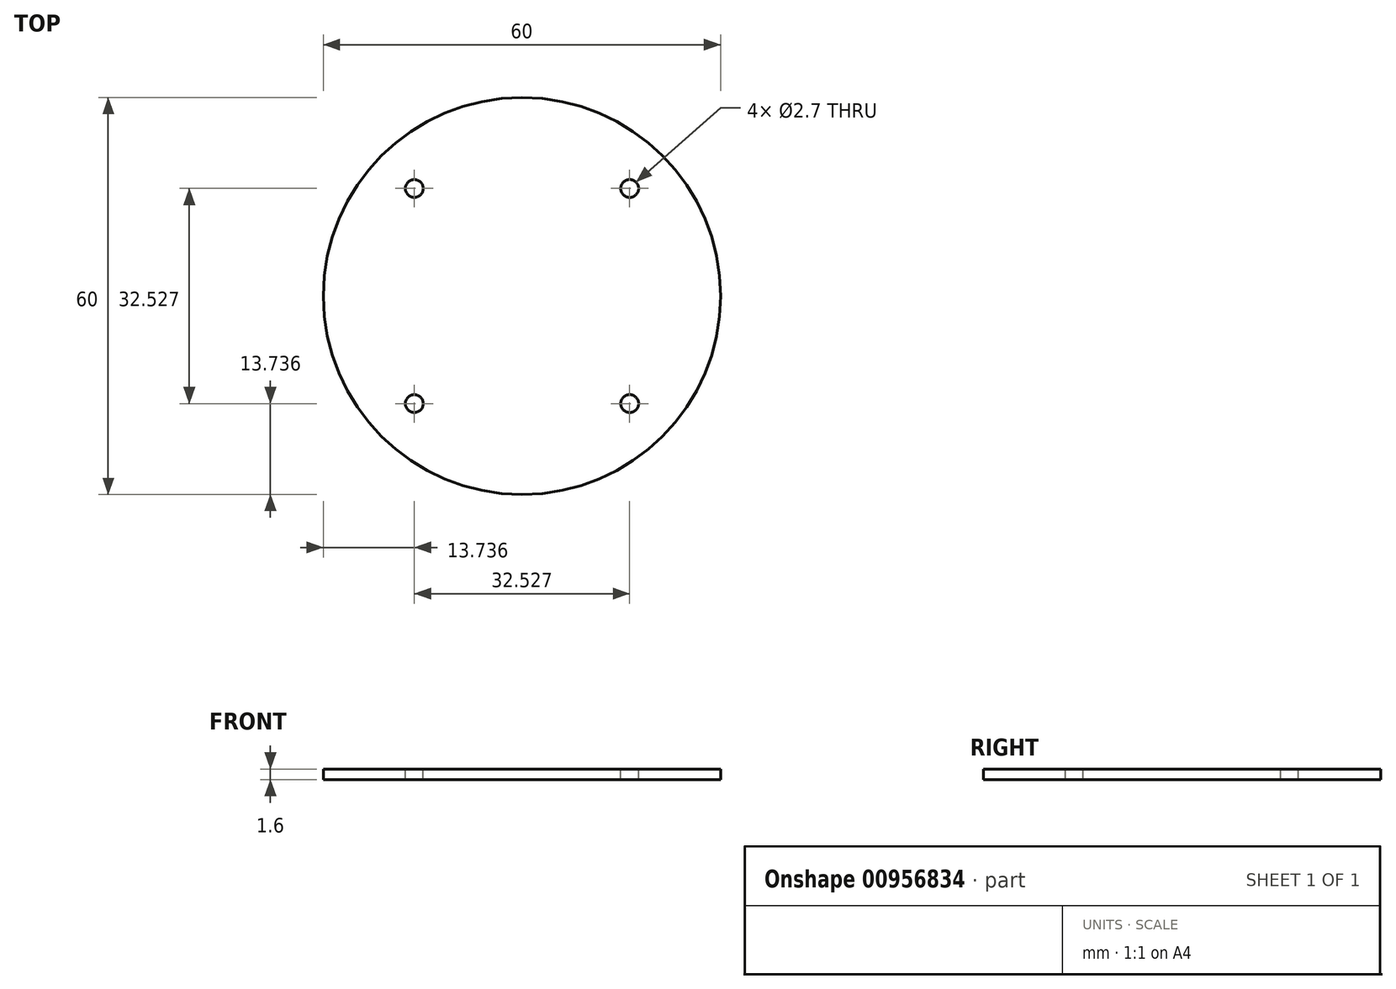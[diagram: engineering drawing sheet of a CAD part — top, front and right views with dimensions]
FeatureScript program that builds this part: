
annotation { "Feature Type Name" : "Feature", "Feature Type Description" : "" }
export const myFeature = defineFeature(function(context is Context, id is Id, definition is map)
    precondition{}
    {
        {
            var Q0;
            Q0=qCreatedBy(makeId("Top.planeOp"),FACE);
            var sketch = newSketch(context, id + "F0", { "sketchPlane" : qUnion([Q0])});
            skCircle(sketch, "E0", {"center": v(0, 0) * mm, "radius": 30 * mm});
            skSolve(sketch);
        }
        {
            var Q0;
            Q0=qSketchRegion(id+"F0",true);
            extrude(context, id + "F1", {"entities" : qUnion([Q0]), "depth" : 1.6 * mm, "offsetDistance" : 25.4 * mm});
        }
        {
            var Q0;
            Q0=makeQuery(id+"F1.opExtrude","CAP_FACE",FACE,{"disambiguationData":[OSD([sQuery(id+"F0.wireOp",EDGE,"E0")])],"isStart":false});
            var sketch = newSketch(context, id + "F2", { "sketchPlane" : qUnion([Q0])});
            skCircle(sketch, "E1", {"center": v(-16.26, 16.26) * mm, "radius": 1.35 * mm});
            skLineSegment(sketch, "E2", {"start": v(0, 0) * mm, "end": v(-36.01, 36.01) * mm, "construction": true});
            skCircle(sketch, "E3.1.0", {"center": v(-16.26, -16.26) * mm, "radius": 1.35 * mm});
            skCircle(sketch, "E3.2.0", {"center": v(16.26, -16.26) * mm, "radius": 1.35 * mm});
            skCircle(sketch, "E3.3.0", {"center": v(16.26, 16.26) * mm, "radius": 1.35 * mm});
            skPoint(sketch, "E3.center", {"position": v(0, 0) * mm});
            skSolve(sketch);
        }
        {
            var Q0;
            Q0=qSketchRegion(id+"F2",true);
            extrude(context, id + "F3", {"entities" : qUnion([Q0]), "operationType" : NewBodyOperationType.REMOVE, "oppositeDirection" : true, "depth" : 25 * mm, "offsetDistance" : 25 * mm});
        }
    });
